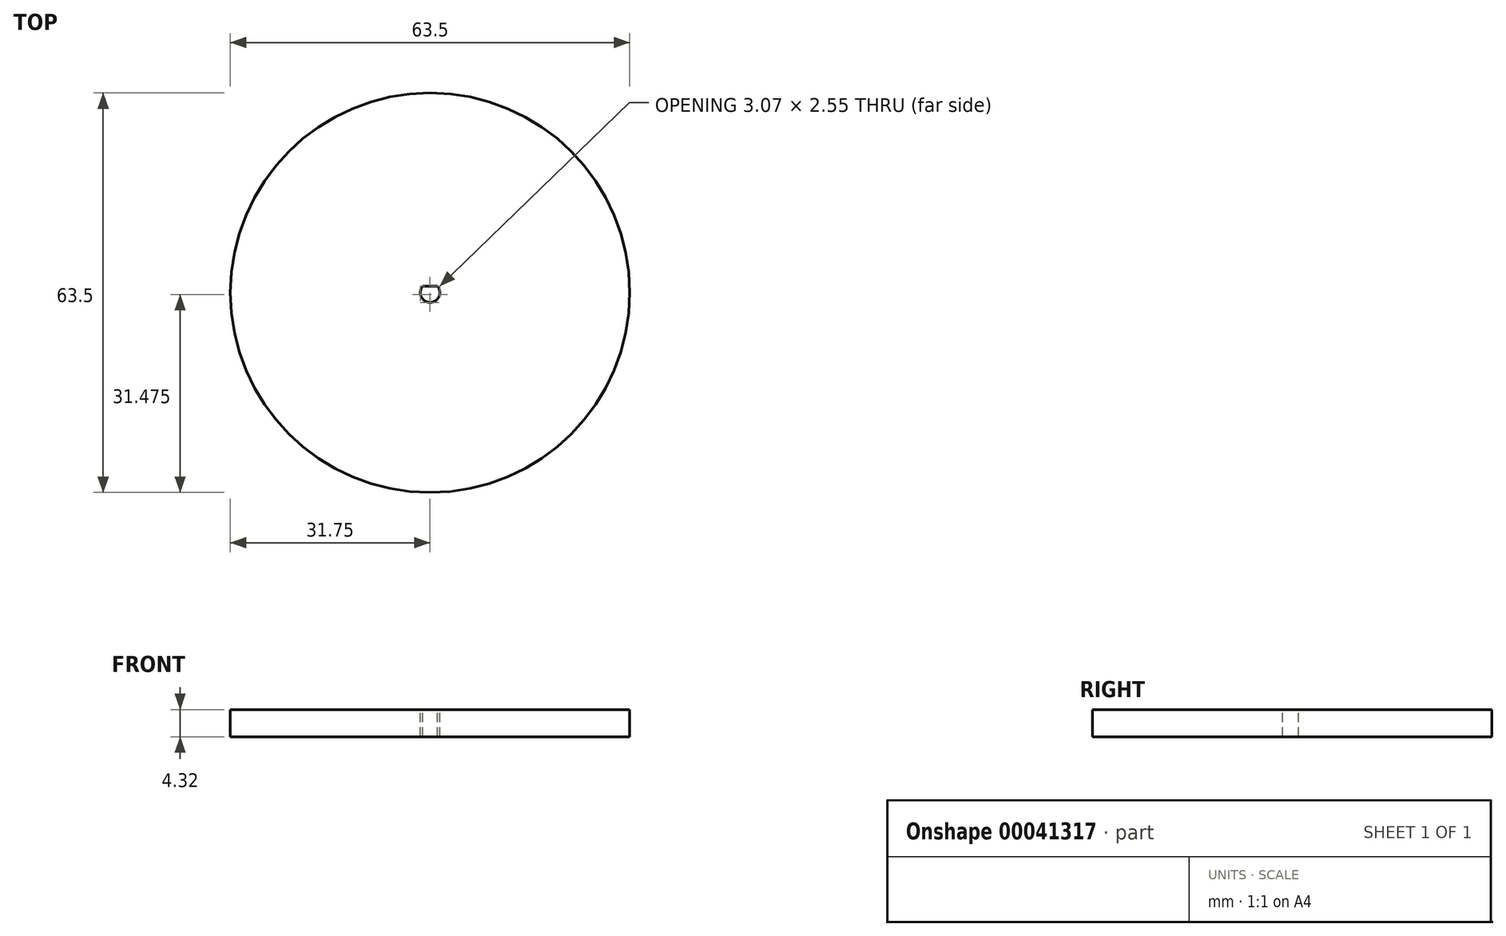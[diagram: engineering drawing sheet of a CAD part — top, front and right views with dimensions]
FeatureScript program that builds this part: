
annotation { "Feature Type Name" : "Feature", "Feature Type Description" : "" }
export const myFeature = defineFeature(function(context is Context, id is Id, definition is map)
    precondition{}
    {
        {
            var Q0;
            Q0=qCreatedBy(makeId("Top.planeOp"),FACE);
            var sketch = newSketch(context, id + "F0", { "sketchPlane" : qUnion([Q0])});
            skCircle(sketch, "E0", {"center": v(0, 0) * mm, "radius": 31.75 * mm});
            skSolve(sketch);
        }
        {
            var Q0;
            Q0 = qSketchRegion(id + "F0", true);
            extrude(context, id + "F1", {"entities" : qUnion([Q0]), "depth" : 4.32 * mm});
        }
        {
            var Q0;
            Q0=makeQuery(id+"F1.opExtrude","CAP_FACE",FACE,{"disambiguationData":[OSD([sQuery(id+"F0.wireOp",EDGE,"E0")])],"isStart":false});
            var sketch = newSketch(context, id + "F2", { "sketchPlane" : qUnion([Q0])});
            skCircle(sketch, "E1", {"center": v(0, 0) * mm, "radius": 1.55 * mm});
            skLineSegment(sketch, "E2", {"start": v(0, -1.55) * mm, "end": v(0, 1) * mm});
            skLineSegment(sketch, "E3", {"start": v(-1.18, 1) * mm, "end": v(1.18, 1) * mm});
            skSolve(sketch);
        }
        {
            var Q0;
            {var subQ3=sQuery(id+"F2.wireOp",EDGE,"E2");Q0=makeQuery(id+"F2.imprint","IMPRINT",FACE,{"disambiguationData":[TD([[makeQuery(id+"F2.imprint","IMPRINT",EDGE,{"derivedFrom":subQ3}),-1.0]])]});}
            var Q1;
            {var subQ3=sQuery(id+"F2.wireOp",EDGE,"E2");Q1=makeQuery(id+"F2.imprint","IMPRINT",FACE,{"disambiguationData":[TD([[makeQuery(id+"F2.imprint","IMPRINT",EDGE,{"derivedFrom":subQ3}),1.0]])]});}
            extrude(context, id + "F3", {"entities" : qUnion([Q0, Q1]), "operationType" : NewBodyOperationType.REMOVE, "endBound" : BoundingType.UP_TO_NEXT, "oppositeDirection" : true, "depth" : 25.4 * mm});
        }
    });
